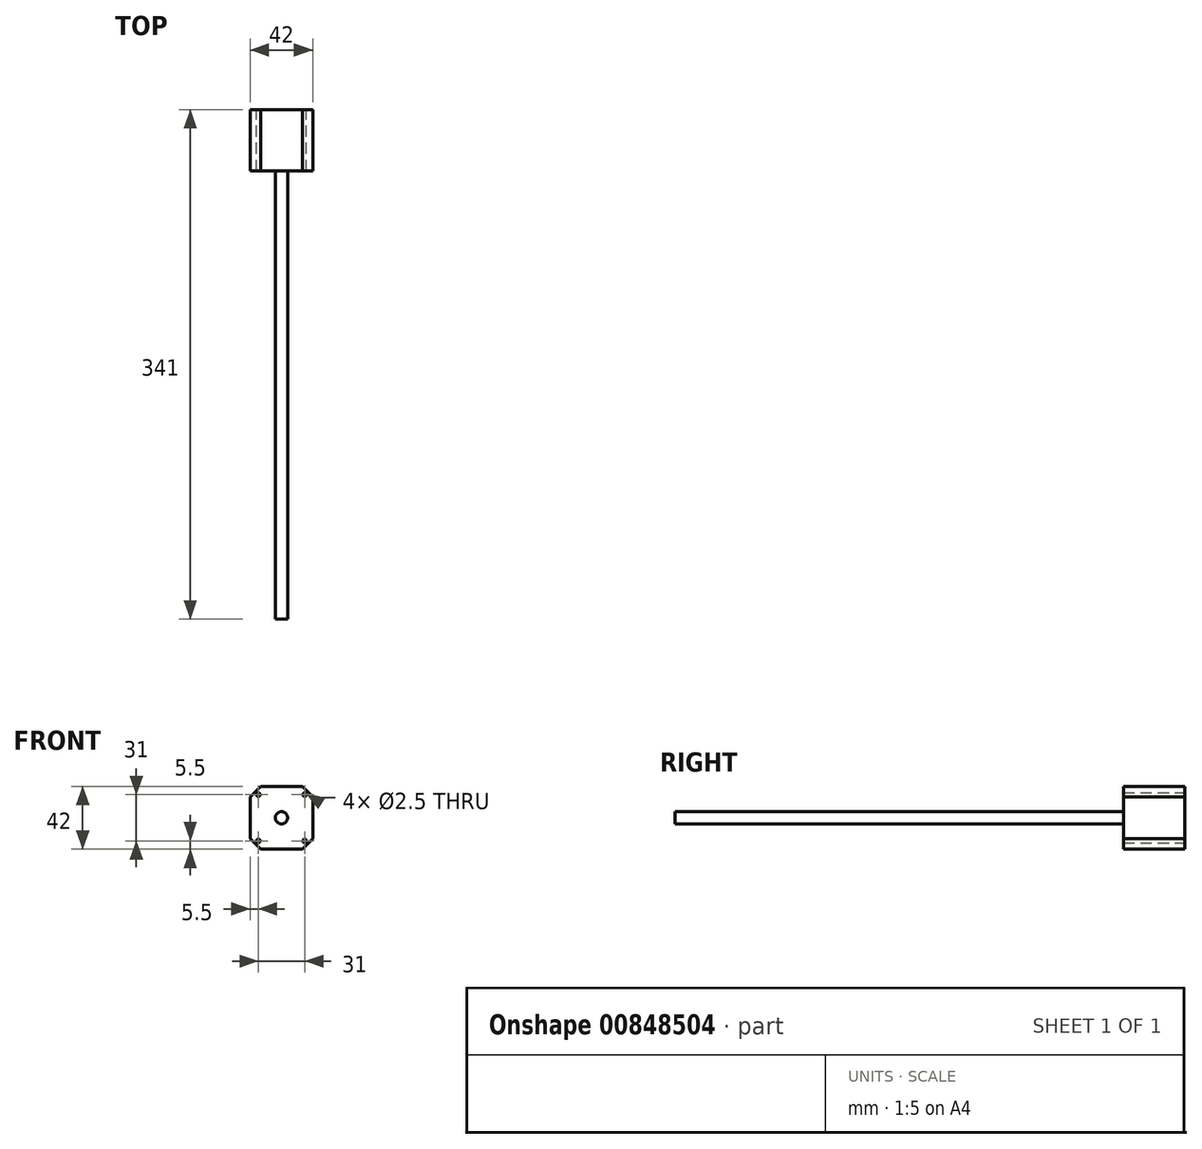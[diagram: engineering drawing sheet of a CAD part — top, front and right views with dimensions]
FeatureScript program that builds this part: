
annotation { "Feature Type Name" : "Feature", "Feature Type Description" : "" }
export const myFeature = defineFeature(function(context is Context, id is Id, definition is map)
    precondition{}
    {
        {
            var Q0;
            Q0=qCreatedBy(makeId("Front.planeOp"),FACE);
            var sketch = newSketch(context, id + "F0", { "sketchPlane" : qUnion([Q0])});
            skLineSegment(sketch, "E0.bottom", {"start": v(21, 21) * mm, "end": v(-21, 21) * mm});
            skLineSegment(sketch, "E0.top", {"start": v(21, -21) * mm, "end": v(-21, -21) * mm});
            skLineSegment(sketch, "E0.left", {"start": v(21, 21) * mm, "end": v(21, -21) * mm});
            skLineSegment(sketch, "E0.right", {"start": v(-21, 21) * mm, "end": v(-21, -21) * mm});
            skPoint(sketch, "E0.middle", {"position": v(0, 0) * mm});
            skCircle(sketch, "E1", {"center": v(0, 0) * mm, "radius": 4.1 * mm});
            skLineSegment(sketch, "E2", {"start": v(-21, 14) * mm, "end": v(-14, 21) * mm});
            skLineSegment(sketch, "E3", {"start": v(14, 21) * mm, "end": v(21, 14) * mm});
            skLineSegment(sketch, "E4", {"start": v(14, -21) * mm, "end": v(21, -14) * mm});
            skLineSegment(sketch, "E5", {"start": v(-21, -14) * mm, "end": v(-14, -21) * mm});
            skCircle(sketch, "E6", {"center": v(-15.5, -15.5) * mm, "radius": 1.25 * mm});
            skCircle(sketch, "E7", {"center": v(15.5, -15.5) * mm, "radius": 1.25 * mm});
            skCircle(sketch, "E8", {"center": v(15.5, 15.5) * mm, "radius": 1.25 * mm});
            skCircle(sketch, "E9", {"center": v(-15.5, 15.5) * mm, "radius": 1.25 * mm});
            skSolve(sketch);
        }
        {
            var Q0;
            Q0=makeQuery(id+"F0.imprint","IMPRINT",FACE,{"disambiguationData":[TD([[makeQuery(id+"F0.imprint","IMPRINT",EDGE,{"derivedFrom":sQuery(id+"F0.wireOp",EDGE,"E1")}),-1.0]])]});
            extrude(context, id + "F1", {"entities" : qUnion([Q0]), "depth" : 41 * mm, "offsetDistance" : 25 * mm});
        }
        {
            var Q0;
            Q0=makeQuery(id+"F0.imprint","IMPRINT",FACE,{"disambiguationData":[TD([[makeQuery(id+"F0.imprint","IMPRINT",EDGE,{"derivedFrom":sQuery(id+"F0.wireOp",EDGE,"E1")}),1.0]])]});
            extrude(context, id + "F2", {"entities" : qUnion([Q0]), "operationType" : NewBodyOperationType.ADD, "depth" : 341 * mm, "offsetDistance" : 25 * mm});
        }
    });
